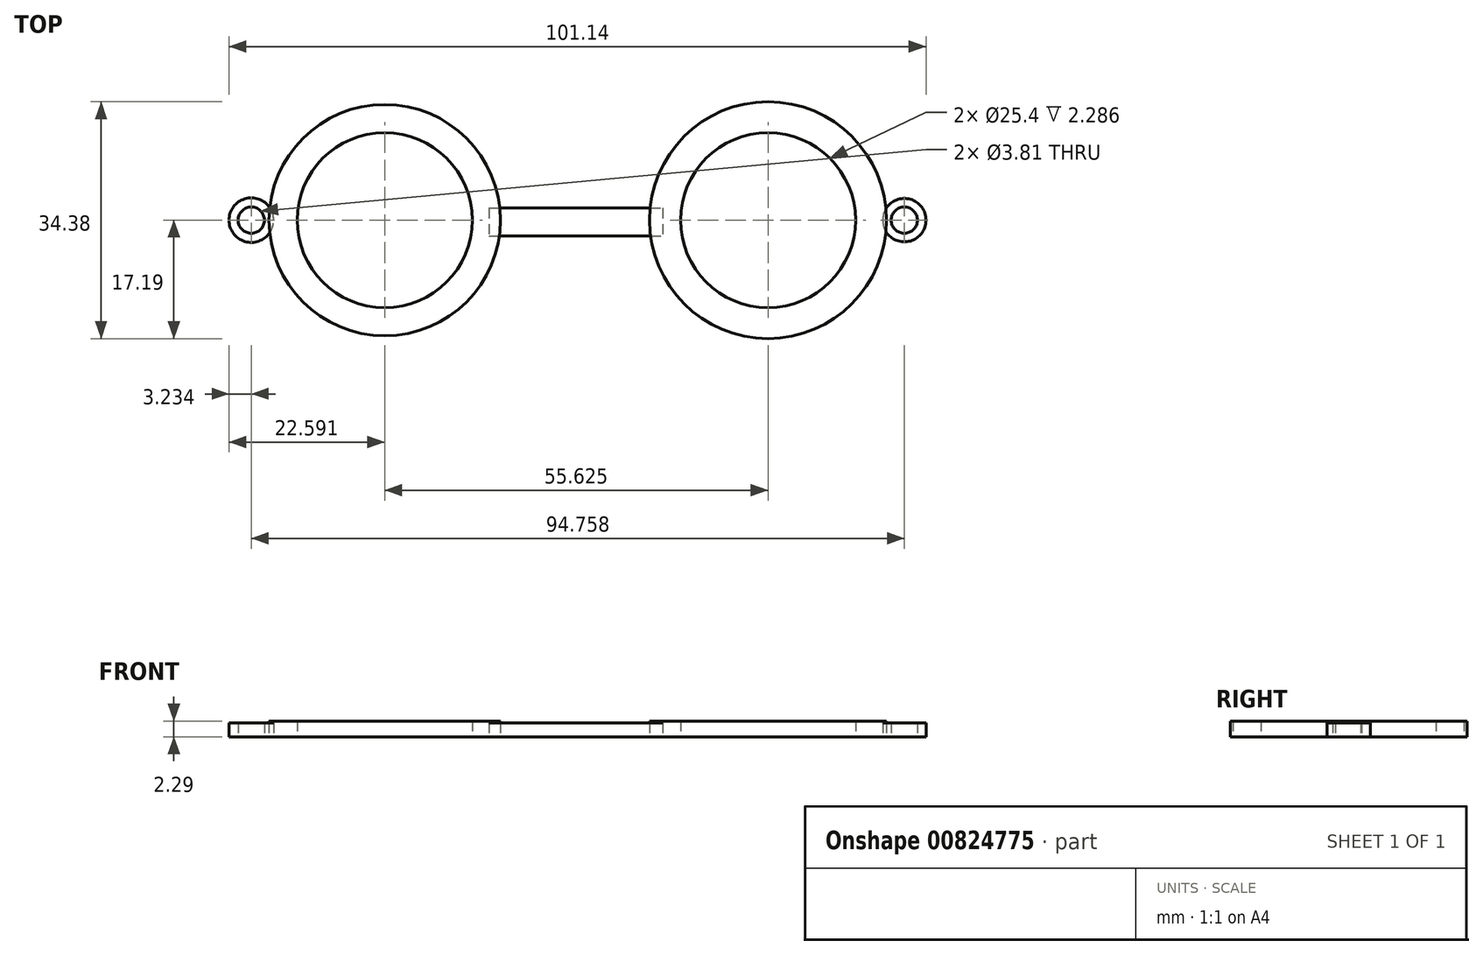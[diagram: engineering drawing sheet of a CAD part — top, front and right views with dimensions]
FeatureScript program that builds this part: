
annotation { "Feature Type Name" : "Feature", "Feature Type Description" : "" }
export const myFeature = defineFeature(function(context is Context, id is Id, definition is map)
    precondition{}
    {
        {
            var Q0;
            Q0=qCreatedBy(makeId("Top.planeOp"),FACE);
            var sketch = newSketch(context, id + "F0", { "sketchPlane" : qUnion([Q0])});
            skCircle(sketch, "E0", {"center": v(-43.97, 0) * mm, "radius": 16.78 * mm});
            skCircle(sketch, "E1", {"center": v(11.66, 0) * mm, "radius": 17.19 * mm});
            skSolve(sketch);
        }
        {
            var Q0;
            Q0=makeQuery(id+"F0.imprint","IMPRINT",FACE,{"disambiguationData":[TD([[makeQuery(id+"F0.imprint","IMPRINT",EDGE,{"derivedFrom":sQuery(id+"F0.wireOp",EDGE,"E0")}),1.0]])]});
            var Q1;
            Q1=makeQuery(id+"F0.imprint","IMPRINT",FACE,{"disambiguationData":[TD([[makeQuery(id+"F0.imprint","IMPRINT",EDGE,{"derivedFrom":sQuery(id+"F0.wireOp",EDGE,"E1")}),1.0]])]});
            extrude(context, id + "F1", {"entities" : qUnion([Q0, Q1]), "depth" : 2.3 * mm, "offsetDistance" : 25.4 * mm});
        }
        {
            var Q0;
            Q0=sQuery(id+"F0.wireOp",VERTEX,"E0.center");
            var Q1;
            Q1=sQuery(id+"F0.wireOp",VERTEX,"E1.center");
            var Q2;
            Q2=makeQuery(id+"F1.opExtrude","SWEPT_BODY",BODY,{"disambiguationData":[OSD([sQuery(id+"F0.wireOp",EDGE,"E0")])]});
            var Q3;
            Q3=makeQuery(id+"F1.opExtrude","SWEPT_BODY",BODY,{"disambiguationData":[OSD([sQuery(id+"F0.wireOp",EDGE,"E1")])]});
            hole(context, id + "F2", {"style" : HoleStyle.SIMPLE, "endStyle" : HoleEndStyle.THROUGH, "oppositeDirection" : true, "holeDiameter" : 25.4 * mm, "majorDiameter" : 6.35 * mm, "isTappedThrough" : true, "tappedDepth" : 12.7 * mm, "tapClearance" : 3, "locations" : qUnion([Q0, Q1]), "scope" : qUnion([Q2, Q3])});
        }
        {
            var Q0;
            Q0=qCreatedBy(makeId("Top.planeOp"),FACE);
            var sketch = newSketch(context, id + "F3", { "sketchPlane" : qUnion([Q0])});
            skCircle(sketch, "E2", {"center": v(-63.33, 0) * mm, "radius": 3.24 * mm});
            skCircle(sketch, "E3", {"center": v(31.43, 0) * mm, "radius": 3.15 * mm});
            skSolve(sketch);
        }
        {
            var Q0;
            Q0=makeQuery(id+"F3.imprint","IMPRINT",FACE,{"disambiguationData":[TD([[makeQuery(id+"F3.imprint","IMPRINT",EDGE,{"derivedFrom":sQuery(id+"F3.wireOp",EDGE,"E2")}),1.0]])]});
            var Q1;
            Q1=makeQuery(id+"F3.imprint","IMPRINT",FACE,{"disambiguationData":[TD([[makeQuery(id+"F3.imprint","IMPRINT",EDGE,{"derivedFrom":sQuery(id+"F3.wireOp",EDGE,"E3")}),1.0]])]});
            extrude(context, id + "F4", {"entities" : qUnion([Q0, Q1]), "depth" : 2.03 * mm, "offsetDistance" : 25.4 * mm});
        }
        {
            var Q0;
            Q0=qCreatedBy(makeId("Front.planeOp"),FACE);
            var sketch = newSketch(context, id + "F5", { "sketchPlane" : qUnion([Q0])});
            skLineSegment(sketch, "E4.bottom", {"start": v(-57.78, 0) * mm, "end": v(-55.2, 0) * mm});
            skLineSegment(sketch, "E4.top", {"start": v(-57.78, -0.89) * mm, "end": v(-55.2, -0.89) * mm});
            skLineSegment(sketch, "E4.left", {"start": v(-57.78, 0) * mm, "end": v(-57.78, -0.89) * mm});
            skLineSegment(sketch, "E4.right", {"start": v(-55.2, 0) * mm, "end": v(-55.2, -0.89) * mm});
            skLineSegment(sketch, "E5.bottom", {"start": v(27.46, 0.69) * mm, "end": v(30.62, 0.69) * mm});
            skLineSegment(sketch, "E5.top", {"start": v(27.46, -0.89) * mm, "end": v(30.62, -0.89) * mm});
            skLineSegment(sketch, "E5.left", {"start": v(27.46, 0.69) * mm, "end": v(27.46, -0.89) * mm});
            skLineSegment(sketch, "E5.right", {"start": v(30.62, 0.69) * mm, "end": v(30.62, -0.89) * mm});
            skSolve(sketch);
        }
        {
            var Q0;
            Q0=sQuery(id+"F3.wireOp",VERTEX,"E2.center");
            var Q1;
            Q1=sQuery(id+"F3.wireOp",VERTEX,"E3.center");
            var Q2;
            Q2=makeQuery(id+"F4.opExtrude","SWEPT_BODY",BODY,{"disambiguationData":[OSD([sQuery(id+"F3.wireOp",EDGE,"E2")])]});
            var Q3;
            Q3=makeQuery(id+"FYcqci6A0Cnqhz6_5.opExtrude","SWEPT_BODY",BODY,{"disambiguationData":[OSD([sQuery(id+"F5.wireOp",EDGE,"E4.bottom"),sQuery(id+"F5.wireOp",EDGE,"E4.top"),sQuery(id+"F5.wireOp",EDGE,"E4.left"),sQuery(id+"F5.wireOp",EDGE,"E4.right")])]});
            var Q4;
            Q4=makeQuery(id+"F4.opExtrude","SWEPT_BODY",BODY,{"disambiguationData":[OSD([sQuery(id+"F3.wireOp",EDGE,"E3")])]});
            var Q5;
            Q5=makeQuery(id+"FYcqci6A0Cnqhz6_5.opExtrude","SWEPT_BODY",BODY,{"disambiguationData":[OSD([sQuery(id+"F5.wireOp",EDGE,"E5.bottom"),sQuery(id+"F5.wireOp",EDGE,"E5.top"),sQuery(id+"F5.wireOp",EDGE,"E5.left"),sQuery(id+"F5.wireOp",EDGE,"E5.right")])]});
            hole(context, id + "F6", {"style" : HoleStyle.SIMPLE, "endStyle" : HoleEndStyle.THROUGH, "oppositeDirection" : true, "holeDiameter" : 3.8 * mm, "majorDiameter" : 6.35 * mm, "isTappedThrough" : true, "tappedDepth" : 12.7 * mm, "tapClearance" : 3, "locations" : qUnion([Q0, Q1]), "scope" : qUnion([Q2, Q3, Q4, Q5])});
        }
        {
            var Q0;
            Q0=qCreatedBy(makeId("Top.planeOp"),FACE);
            var sketch = newSketch(context, id + "F7", { "sketchPlane" : qUnion([Q0])});
            skLineSegment(sketch, "E6.bottom", {"start": v(-28.85, 1.75) * mm, "end": v(-3.6, 1.75) * mm});
            skLineSegment(sketch, "E6.top", {"start": v(-28.85, -2.3) * mm, "end": v(-3.6, -2.3) * mm});
            skLineSegment(sketch, "E6.left", {"start": v(-28.85, 1.75) * mm, "end": v(-28.85, -2.3) * mm});
            skLineSegment(sketch, "E6.right", {"start": v(-3.6, 1.75) * mm, "end": v(-3.6, -2.3) * mm});
            skSolve(sketch);
        }
        {
            var Q0;
            Q0 = qSketchRegion(id + "F7", true);
            extrude(context, id + "F8", {"entities" : qUnion([Q0]), "depth" : 2.03 * mm, "offsetDistance" : 25.4 * mm});
        }
    });
